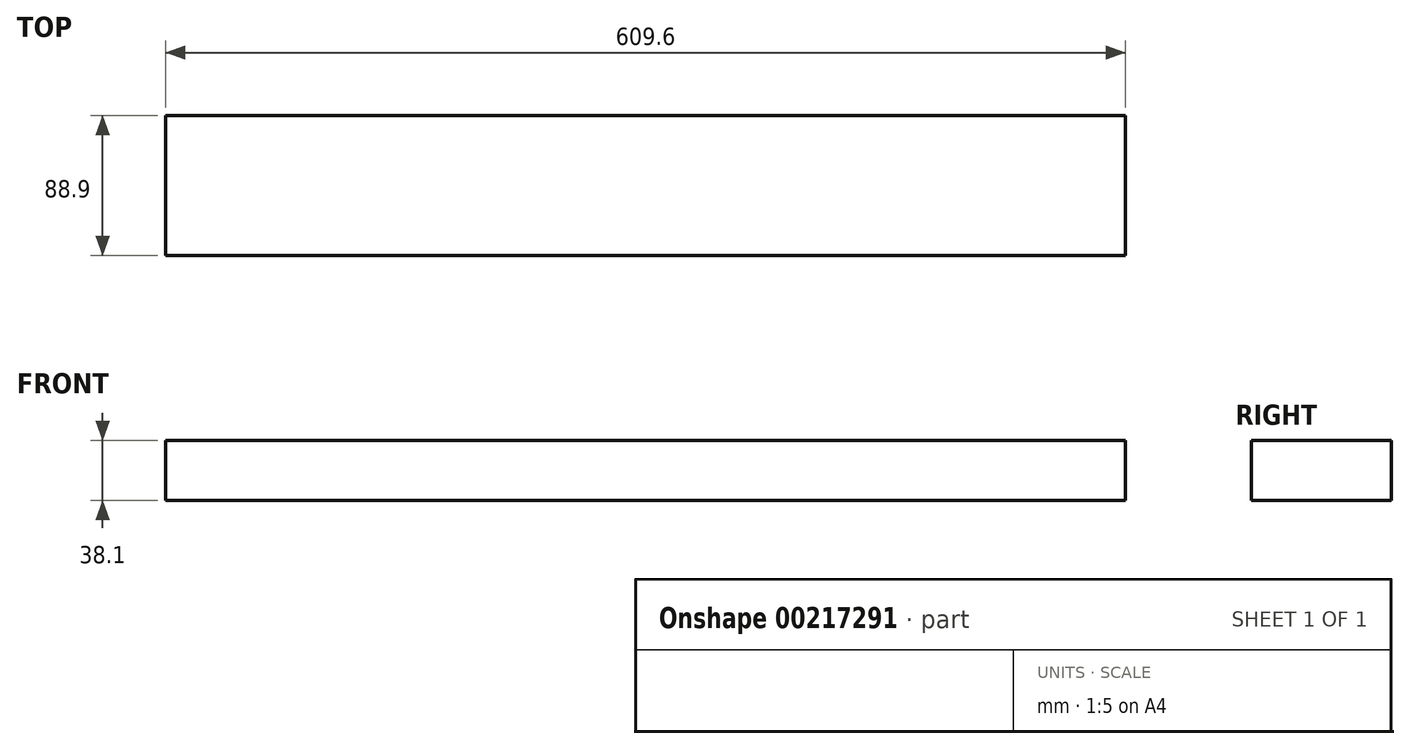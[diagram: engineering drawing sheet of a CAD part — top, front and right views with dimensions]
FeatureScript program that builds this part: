
annotation { "Feature Type Name" : "Feature", "Feature Type Description" : "" }
export const myFeature = defineFeature(function(context is Context, id is Id, definition is map)
    precondition{}
    {
        {
            var Q0;
            Q0=qCreatedBy(makeId("Right.planeOp"),FACE);
            var sketch = newSketch(context, id + "F0", { "sketchPlane" : qUnion([Q0])});
            skLineSegment(sketch, "E0.bottom", {"start": v(44.45, 19.05) * mm, "end": v(-44.45, 19.05) * mm});
            skLineSegment(sketch, "E0.top", {"start": v(44.45, -19.05) * mm, "end": v(-44.45, -19.05) * mm});
            skLineSegment(sketch, "E0.left", {"start": v(44.45, 19.05) * mm, "end": v(44.45, -19.05) * mm});
            skLineSegment(sketch, "E0.right", {"start": v(-44.45, 19.05) * mm, "end": v(-44.45, -19.05) * mm});
            skPoint(sketch, "E0.middle", {"position": v(0, 0) * mm});
            skSolve(sketch);
        }
        {
            var Q0;
            Q0=makeQuery(id+"F0.imprint","IMPRINT",FACE,{"disambiguationData":[TD([[makeQuery(id+"F0.imprint","IMPRINT",EDGE,{"derivedFrom":sQuery(id+"F0.wireOp",EDGE,"E0.bottom")}),1.0]])]});
            extrude(context, id + "F1", {"entities" : qUnion([Q0]), "depth" : 609.6 * mm});
        }
    });
